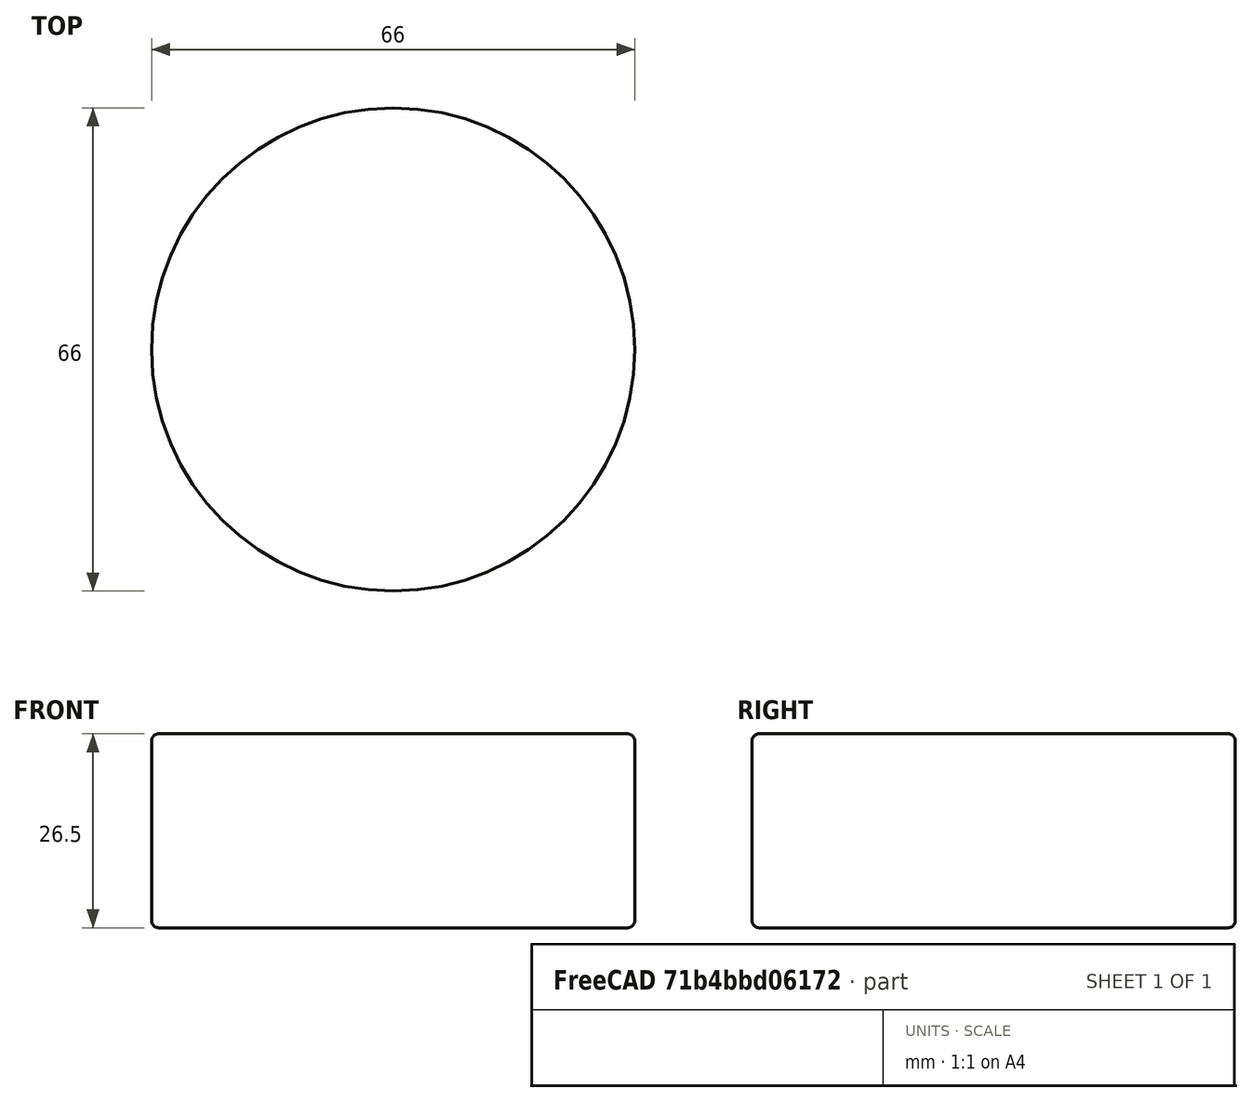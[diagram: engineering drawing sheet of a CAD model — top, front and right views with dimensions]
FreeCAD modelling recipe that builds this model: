
FCSTD DOCUMENT  (FreeCAD 0.18R16131 (Git))
Label: RealWheel
License: All rights reserved
LicenseURL: http://en.wikipedia.org/wiki/All_rights_reserved
objects: PartDesign::Fillet×2, Sketcher::SketchObject×1, PartDesign::Pad×1, PartDesign::Body×1
note: 6 computed .brp shape members not serialized (recipe doc carries the construction recipe); baked Part::Feature solids carry a one-line shape summary decoded from their .brp

FEATURE [Sketcher::SketchObject] Sketch
  MapMode = 5
  Support = -> [XY_Plane]
  sketch-geometry (1):
    g0: Circle CenterX=0 CenterY=0 CenterZ=0 NormalX=0 NormalY=0 NormalZ=1 AngleXU=0 Radius=33
  constraints (1):
    c: Radius(g0) = 33
FEATURE [PartDesign::Pad] Pad
  Length = 26.5
  Length2 = 100
  Profile = -> Sketch
  Type = 0
FEATURE [PartDesign::Fillet] Fillet
  Base = -> Pad [Edge2]
  BaseFeature = -> Pad
  Radius = 1
FEATURE [PartDesign::Fillet] Fillet001
  Base = -> Fillet [Edge3]
  BaseFeature = -> Fillet
  Radius = 1
FEATURE [PartDesign::Body] Body
  Group = -> [Sketch,Pad,Fillet,Fillet001]
  Origin = -> Origin
  Tip = -> Fillet001
